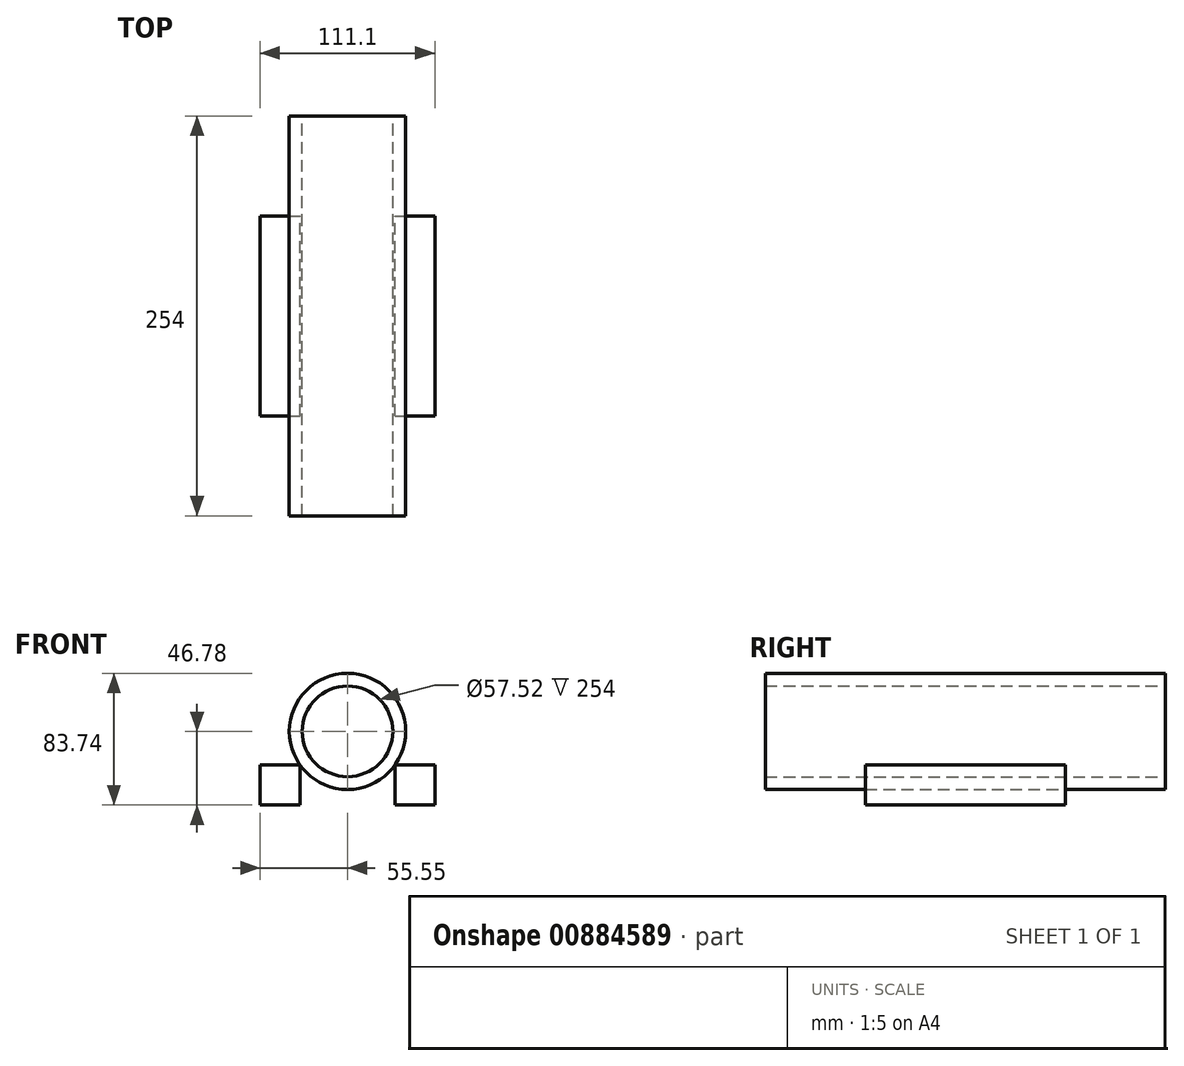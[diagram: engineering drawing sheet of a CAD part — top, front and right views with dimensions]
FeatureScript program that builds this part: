
annotation { "Feature Type Name" : "Feature", "Feature Type Description" : "" }
export const myFeature = defineFeature(function(context is Context, id is Id, definition is map)
    precondition{}
    {
        {
            var Q0;
            Q0=qCreatedBy(makeId("Right.planeOp"),FACE);
            var sketch = newSketch(context, id + "F0", { "sketchPlane" : qUnion([Q0])});
            skLineSegment(sketch, "E0", {"start": v(0, 0) * mm, "end": v(254, 0) * mm});
            skSolve(sketch);
        }
        {
            var Q0;
            Q0=qCreatedBy(makeId("Front.planeOp"),FACE);
            var sketch = newSketch(context, id + "F1", { "sketchPlane" : qUnion([Q0])});
            skCircle(sketch, "E1", {"center": v(0, 0) * mm, "radius": 28.76 * mm});
            skCircle(sketch, "E2", {"center": v(0, 0) * mm, "radius": 36.96 * mm});
            skSolve(sketch);
        }
        {
            var Q0;
            Q0=makeQuery(id+"F1.imprint","IMPRINT",FACE,{"disambiguationData":[TD([[makeQuery(id+"F1.imprint","IMPRINT",EDGE,{"derivedFrom":sQuery(id+"F1.wireOp",EDGE,"E1")}),-1.0]])]});
            var Q1;
            Q1=sQuery(id+"F0.wireOp",EDGE,"E0");
            sweep(context, id + "F2", {"profiles" : qUnion([Q0]), "path" : qUnion([Q1])});
        }
        {
            var Q0;
            Q0=qCreatedBy(makeId("Front.planeOp"),FACE);
            cPlane(context, id + "F3", {"entities" : qUnion([Q0]), "cplaneType" : CPlaneType.OFFSET, "offset" : 127 * mm, "oppositeDirection" : true, "width" : 152.4 * mm, "height" : 152.4 * mm});
        }
        {
            var Q0;
            Q0=qCreatedBy(id+"F3.planeOp",FACE);
            var sketch = newSketch(context, id + "F4", { "sketchPlane" : qUnion([Q0])});
            skLineSegment(sketch, "E3.bottom", {"start": v(-55.55, -21.38) * mm, "end": v(-30.15, -21.38) * mm});
            skLineSegment(sketch, "E3.top", {"start": v(-55.55, -46.78) * mm, "end": v(-30.15, -46.78) * mm});
            skLineSegment(sketch, "E3.left", {"start": v(-55.55, -21.38) * mm, "end": v(-55.55, -46.78) * mm});
            skLineSegment(sketch, "E3.right", {"start": v(-30.15, -21.38) * mm, "end": v(-30.15, -46.78) * mm});
            skLineSegment(sketch, "E4.bottom", {"start": v(30.15, -21.38) * mm, "end": v(55.55, -21.38) * mm});
            skLineSegment(sketch, "E4.top", {"start": v(30.15, -46.78) * mm, "end": v(55.55, -46.78) * mm});
            skLineSegment(sketch, "E4.left", {"start": v(30.15, -21.38) * mm, "end": v(30.15, -46.78) * mm});
            skLineSegment(sketch, "E4.right", {"start": v(55.55, -21.38) * mm, "end": v(55.55, -46.78) * mm});
            skLineSegment(sketch, "E5", {"start": v(-30.15, -46.78) * mm, "end": v(30.15, -46.78) * mm, "construction": true});
            skSolve(sketch);
        }
        {
            var Q0;
            Q0=makeQuery(id+"F4.imprint","IMPRINT",FACE,{"disambiguationData":[TD([[makeQuery(id+"F4.imprint","IMPRINT",EDGE,{"derivedFrom":sQuery(id+"F4.wireOp",EDGE,"E4.bottom")}),-1.0]])]});
            var Q1;
            Q1=makeQuery(id+"F4.imprint","IMPRINT",FACE,{"disambiguationData":[TD([[makeQuery(id+"F4.imprint","IMPRINT",EDGE,{"derivedFrom":sQuery(id+"F4.wireOp",EDGE,"E3.bottom")}),-1.0]])]});
            extrude(context, id + "F5", {"entities" : qUnion([Q0, Q1]), "depth" : 63.5 * mm, "offsetDistance" : 25.4 * mm, "hasSecondDirection" : true, "secondDirectionOppositeDirection" : true, "secondDirectionDepth" : 63.5 * mm});
        }
    });
